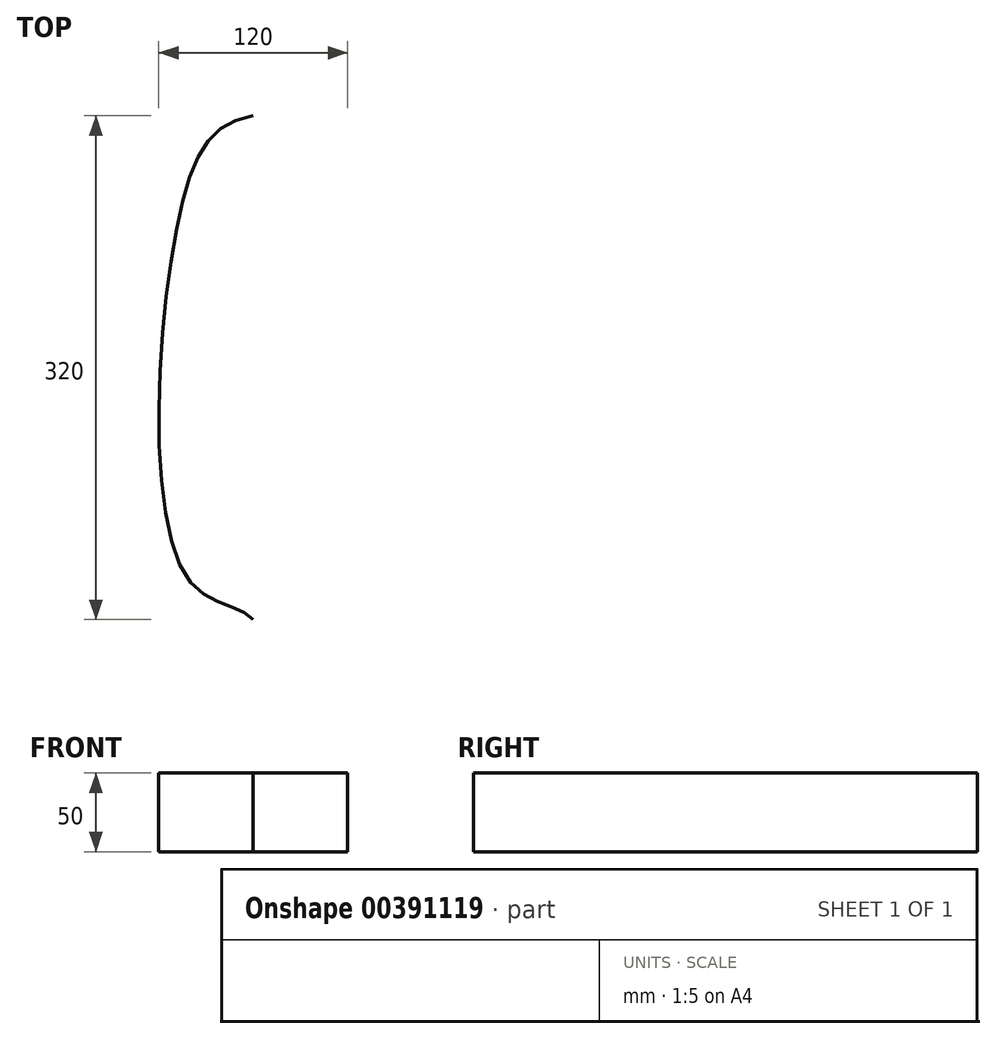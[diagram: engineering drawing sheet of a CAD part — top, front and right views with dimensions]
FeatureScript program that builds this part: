
annotation { "Feature Type Name" : "Feature", "Feature Type Description" : "" }
export const myFeature = defineFeature(function(context is Context, id is Id, definition is map)
    precondition{}
    {
        {
            var Q0;
            Q0=qCreatedBy(makeId("Top.planeOp"),FACE);
            var sketch = newSketch(context, id + "F0", { "sketchPlane" : qUnion([Q0])});
            skFitSpline(sketch, "E0", {"points": [v(0, 0) * mm, v(40.6, 24.64) * mm, v(47.75, 253.27) * mm, v(0, 320) * mm], "startDerivative": vector(108.21, 132.25) * mm, "endDerivative": vector(-286.87, 39.83) * mm});
            skLineSegment(sketch, "E1", {"start": v(60, 0) * mm, "end": v(60, 127.7) * mm, "construction": true});
            skLineSegment(sketch, "E2", {"start": v(0, 320) * mm, "end": v(0, 0) * mm, "construction": true});
            skFitSpline(sketch, "E3.MirrorCS", {"points": [v(0, 0) * mm, v(-40.6, 24.64) * mm, v(-47.75, 253.27) * mm, v(0, 320) * mm], "startDerivative": vector(-108.21, 132.25) * mm, "endDerivative": vector(286.87, 39.83) * mm});
            skSolve(sketch);
        }
        {
            var Q0;
            Q0=makeQuery(id+"F0.imprint","IMPRINT",FACE,{"disambiguationData":[TD([[makeQuery(id+"F0.imprint","IMPRINT",EDGE,{"derivedFrom":sQuery(id+"F0.wireOp",EDGE,"E0")}),1.0]])]});
            extrude(context, id + "F1", {"entities" : qUnion([Q0]), "depth" : 50 * mm});
        }
    });
